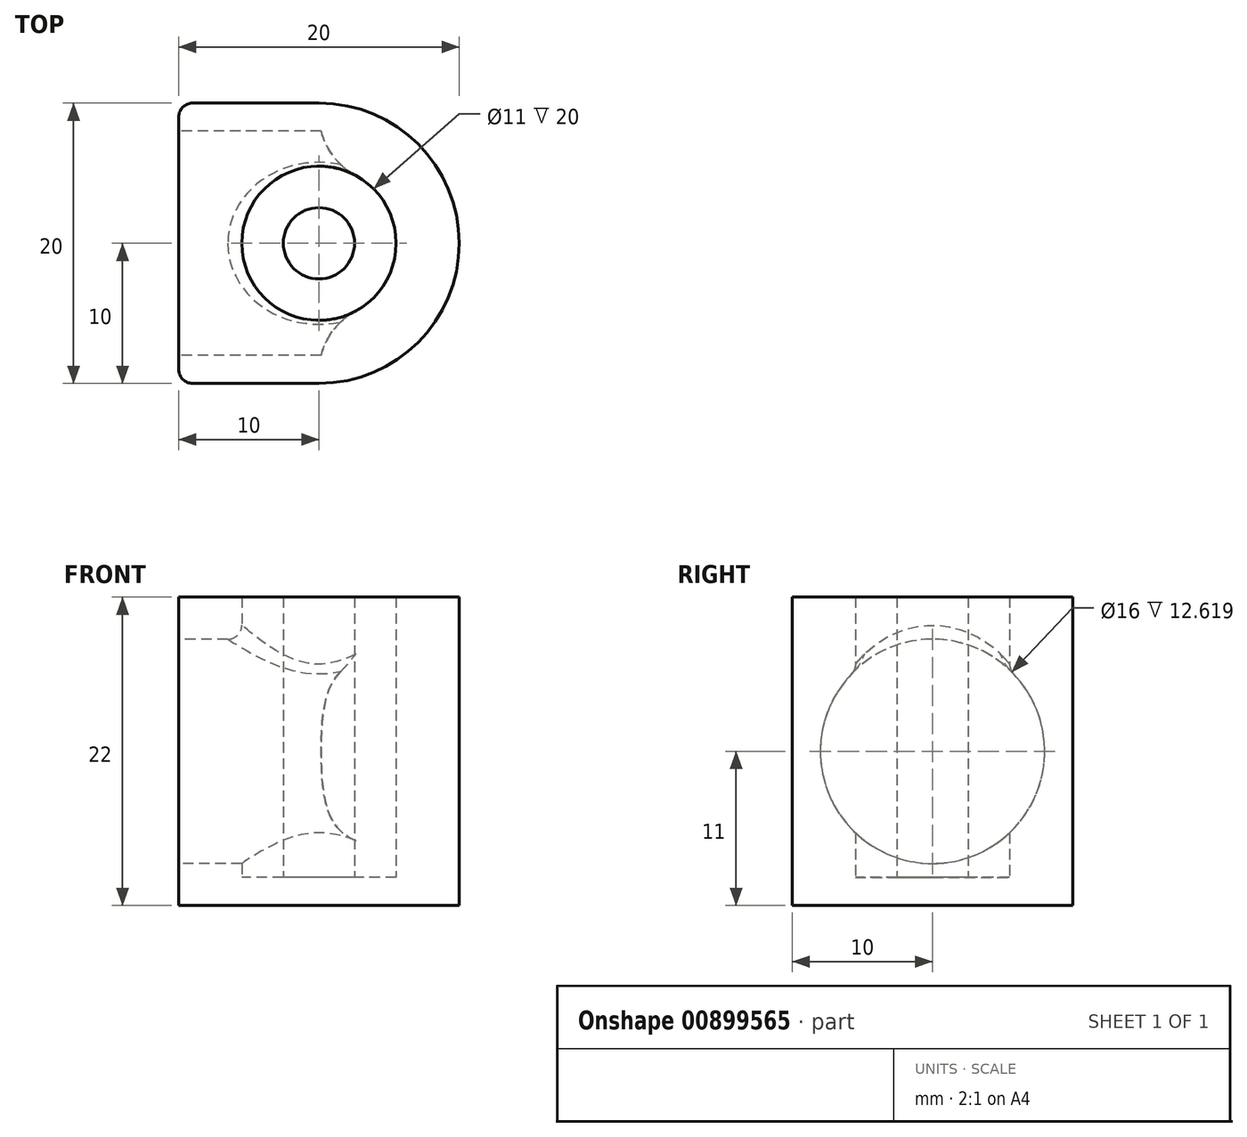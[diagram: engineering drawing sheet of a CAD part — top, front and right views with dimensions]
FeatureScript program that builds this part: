
annotation { "Feature Type Name" : "Feature", "Feature Type Description" : "" }
export const myFeature = defineFeature(function(context is Context, id is Id, definition is map)
    precondition{}
    {
        {
            var Q0;
            Q0=qCreatedBy(makeId("Top.planeOp"),FACE);
            var sketch = newSketch(context, id + "F0", { "sketchPlane" : qUnion([Q0])});
            skCircle(sketch, "E0", {"center": v(0, 0) * mm, "radius": 5.5 * mm});
            skArc(sketch, "E1", {"start": v(0, -10) * mm, "mid": v(10, 0) * mm, "end": v(0, 10) * mm});
            skLineSegment(sketch, "E2", {"start": v(0, 10) * mm, "end": v(-10, 10) * mm});
            skLineSegment(sketch, "E3", {"start": v(0, -10) * mm, "end": v(-10, -10) * mm});
            skLineSegment(sketch, "E4", {"start": v(-10, -10) * mm, "end": v(-10, 10) * mm});
            skCircle(sketch, "E5", {"center": v(0, 0) * mm, "radius": 2.54 * mm});
            skSolve(sketch);
        }
        {
            var Q0;
            Q0=makeQuery(id+"F0.imprint","IMPRINT",FACE,{"disambiguationData":[TD([[makeQuery(id+"F0.imprint","IMPRINT",EDGE,{"derivedFrom":sQuery(id+"F0.wireOp",EDGE,"E0")}),-1.0]])]});
            extrude(context, id + "F1", {"entities" : qUnion([Q0]), "depth" : 22 * mm, "offsetDistance" : 25 * mm});
        }
        {
            var Q0;
            Q0=makeQuery(id+"F0.imprint","IMPRINT",FACE,{"disambiguationData":[TD([[makeQuery(id+"F0.imprint","IMPRINT",EDGE,{"derivedFrom":sQuery(id+"F0.wireOp",EDGE,"E0")}),1.0]])]});
            extrude(context, id + "F2", {"entities" : qUnion([Q0]), "operationType" : NewBodyOperationType.ADD, "depth" : 2 * mm, "offsetDistance" : 25 * mm});
        }
        {
            var Q0;
            Q0=makeQuery(id+"F1.opExtrude","SWEPT_FACE",FACE,{"disambiguationData":[OSD([sQuery(id+"F0.wireOp",EDGE,"E4")])]});
            var sketch = newSketch(context, id + "F3", { "sketchPlane" : qUnion([Q0])});
            skLineSegment(sketch, "E6", {"start": v(10, 22) * mm, "end": v(-10, 0) * mm, "construction": true});
            skLineSegment(sketch, "E7", {"start": v(-10, 22) * mm, "end": v(10, 0) * mm, "construction": true});
            skCircle(sketch, "E8", {"center": v(0, 11) * mm, "radius": 8 * mm});
            skSolve(sketch);
        }
        {
            var Q0;
            Q0=makeQuery(id+"F3.imprint","IMPRINT",FACE,{"disambiguationData":[TD([[makeQuery(id+"F3.imprint","IMPRINT",EDGE,{"derivedFrom":sQuery(id+"F3.wireOp",EDGE,"E8")}),1.0]])]});
            extrude(context, id + "F4", {"entities" : qUnion([Q0]), "operationType" : NewBodyOperationType.REMOVE, "oppositeDirection" : true, "depth" : 10 * mm, "offsetDistance" : 25 * mm});
        }
        {
            var Q0;
            Q0=makeQuery(id+"F0.imprint","IMPRINT",FACE,{"disambiguationData":[TD([[makeQuery(id+"F0.imprint","IMPRINT",EDGE,{"derivedFrom":sQuery(id+"F0.wireOp",EDGE,"E5")}),1.0]])]});
            var Q1;
            Q1=sQuery(id+"F0.wireOp",EDGE,"E5");
            extrude(context, id + "F5", {"entities" : qUnion([Q0]), "operationType" : NewBodyOperationType.ADD, "surfaceEntities" : qUnion([Q1]), "depth" : 22 * mm, "offsetDistance" : 25 * mm});
        }
        {
            var Q0;
            Q0=makeQuery(id+"F1.opExtrude","SWEPT_EDGE",EDGE,{"disambiguationData":[OSD([sQuery(id+"F0.wireOp",EDGE,"E3"),sQuery(id+"F0.wireOp",EDGE,"E4")])]});
            var Q1;
            Q1=makeQuery(id+"F1.opExtrude","SWEPT_EDGE",EDGE,{"disambiguationData":[OSD([sQuery(id+"F0.wireOp",EDGE,"E2"),sQuery(id+"F0.wireOp",EDGE,"E4")])]});
            var Q2;
            Q2=makeQuery(id+"F4.boolean.opBoolean","INTERSECT",EDGE,{"disambiguationData":[OD(1.0)],"derivedFrom":[makeQuery(id+"F1.opExtrude","SWEPT_FACE",FACE,{"disambiguationData":[OSD([sQuery(id+"F0.wireOp",EDGE,"E0")])]}),makeQuery(id+"F4.opExtrude","SWEPT_FACE",FACE,{"disambiguationData":[OSD([sQuery(id+"F3.wireOp",EDGE,"E8")])]})]});
            fillet(context, id + "F6", {"entities" : qUnion([Q0, Q1, Q2]), "radius" : 1 * mm, "tangentPropagation" : true, "allowEdgeOverflow" : false});
        }
        {
            var Q0;
            Q0=makeQuery(id+"F4.boolean.opBoolean","INTERSECT",EDGE,{"disambiguationData":[OD(1.0)],"derivedFrom":[makeQuery(id+"F1.opExtrude","SWEPT_FACE",FACE,{"disambiguationData":[OSD([sQuery(id+"F0.wireOp",EDGE,"E0")])]}),makeQuery(id+"F4.opExtrude","CAP_FACE",FACE,{"disambiguationData":[OSD([sQuery(id+"F3.wireOp",EDGE,"E8")])],"isStart":false})]});
            var Q1;
            Q1=makeQuery(id+"F4.boolean.opBoolean","INTERSECT",EDGE,{"disambiguationData":[OD(0.0)],"derivedFrom":[makeQuery(id+"F1.opExtrude","SWEPT_FACE",FACE,{"disambiguationData":[OSD([sQuery(id+"F0.wireOp",EDGE,"E0")])]}),makeQuery(id+"F4.opExtrude","CAP_FACE",FACE,{"disambiguationData":[OSD([sQuery(id+"F3.wireOp",EDGE,"E8")])],"isStart":false})]});
            fillet(context, id + "F7", {"entities" : qUnion([Q0, Q1]), "radius" : 5 * mm, "tangentPropagation" : true, "allowEdgeOverflow" : false});
        }
    });
